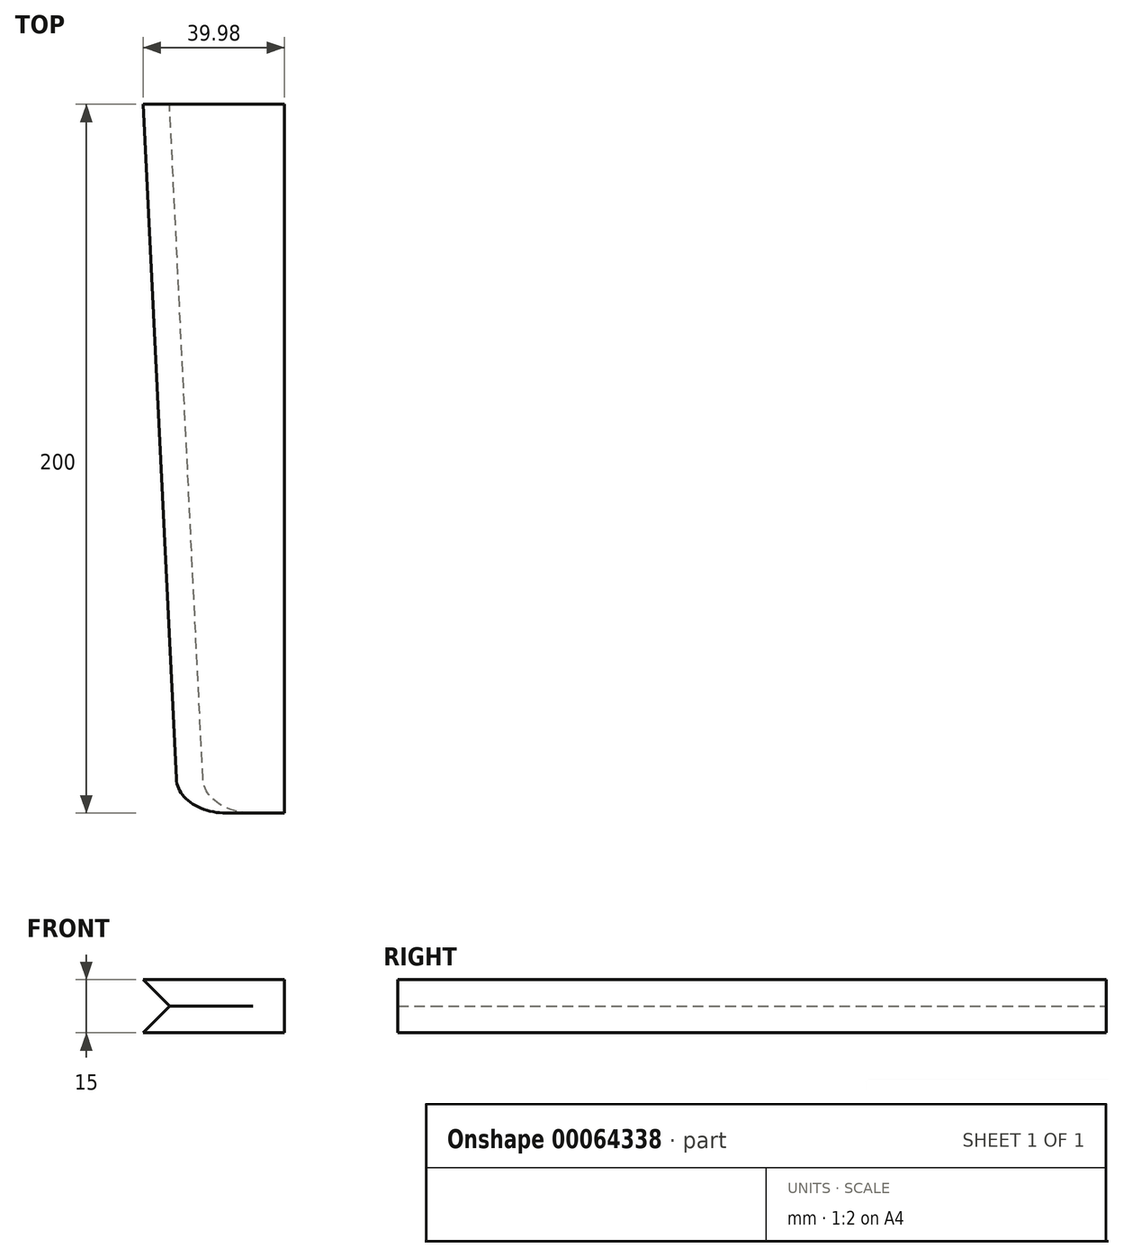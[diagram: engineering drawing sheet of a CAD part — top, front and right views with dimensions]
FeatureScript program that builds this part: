
annotation { "Feature Type Name" : "Feature", "Feature Type Description" : "" }
export const myFeature = defineFeature(function(context is Context, id is Id, definition is map)
    precondition{}
    {
        {
            var Q0;
            Q0=qCreatedBy(makeId("Front.planeOp"),FACE);
            var sketch = newSketch(context, id + "F0", { "sketchPlane" : qUnion([Q0])});
            skLineSegment(sketch, "E0", {"start": v(0, 0) * mm, "end": v(0, 15) * mm});
            skLineSegment(sketch, "E1", {"start": v(0, 15) * mm, "end": v(-40, 15) * mm});
            skLineSegment(sketch, "E2", {"start": v(-40, 15) * mm, "end": v(-32.5, 7.5) * mm});
            skLineSegment(sketch, "E3", {"start": v(-25, 0) * mm, "end": v(0, 0) * mm});
            skLineSegment(sketch, "E4", {"start": v(-32.5, 7.5) * mm, "end": v(-40, 0) * mm});
            skLineSegment(sketch, "E5", {"start": v(-40, 0) * mm, "end": v(-25, 0) * mm});
            skSolve(sketch);
        }
        {
            var Q0;
            Q0=makeQuery(id+"F0.imprint","IMPRINT",FACE,{"disambiguationData":[TD([[makeQuery(id+"F0.imprint","IMPRINT",EDGE,{"derivedFrom":sQuery(id+"F0.wireOp",EDGE,"E0")}),1.0]])]});
            extrude(context, id + "F1", {"entities" : qUnion([Q0]), "depth" : 200 * mm});
        }
        {
            var Q0;
            Q0=makeQuery(id+"F1.opExtrude","CAP_EDGE",EDGE,{"disambiguationData":[OSD([sQuery(id+"F0.wireOp",EDGE,"E2")])],"isStart":false});
            var Q1;
            Q1=makeQuery(id+"F1.opExtrude","CAP_EDGE",EDGE,{"disambiguationData":[OSD([sQuery(id+"F0.wireOp",EDGE,"E4")])],"isStart":false});
            chamfer(context, id + "F2", {"entities" : qUnion([Q0, Q1]), "chamferType" : ChamferType.OFFSET_ANGLE, "width" : 7 * mm, "oppositeDirection" : false, "angle" : 88 * degree, "tangentPropagation" : true});
        }
        {
            var Q0;
            {var subQ0=sQuery(id+"F0.wireOp",EDGE,"E2");Q0=makeQuery(id+"F2.opChamfer","BLEND_EDGE",EDGE,{"blendedFrom":[makeQuery(id+"F1.opExtrude","CAP_EDGE",EDGE,{"disambiguationData":[OSD([subQ0])],"isStart":false}),makeQuery(id+"F1.opExtrude","CAP_FACE",FACE,{"disambiguationData":[OSD([sQuery(id+"F0.wireOp",EDGE,"E0"),sQuery(id+"F0.wireOp",EDGE,"E1"),subQ0,sQuery(id+"F0.wireOp",EDGE,"E3")])],"isStart":false})],"blendedInto":[makeQuery(id+"F1.opExtrude","CAP_FACE",FACE,{"disambiguationData":[OSD([sQuery(id+"F0.wireOp",EDGE,"E0"),sQuery(id+"F0.wireOp",EDGE,"E1"),subQ0,sQuery(id+"F0.wireOp",EDGE,"E3")])],"isStart":false})]});}
            var Q1;
            {var subQ0=sQuery(id+"F0.wireOp",EDGE,"E4");Q1=makeQuery(id+"F2.opChamfer","BLEND_EDGE",EDGE,{"blendedFrom":[makeQuery(id+"F1.opExtrude","CAP_EDGE",EDGE,{"disambiguationData":[OSD([subQ0])],"isStart":false}),makeQuery(id+"F1.opExtrude","CAP_FACE",FACE,{"disambiguationData":[OSD([sQuery(id+"F0.wireOp",EDGE,"E0"),sQuery(id+"F0.wireOp",EDGE,"E1"),sQuery(id+"F0.wireOp",EDGE,"E2"),sQuery(id+"F0.wireOp",EDGE,"E3"),subQ0,sQuery(id+"F0.wireOp",EDGE,"E5")])],"isStart":false})],"blendedInto":[makeQuery(id+"F1.opExtrude","CAP_FACE",FACE,{"disambiguationData":[OSD([sQuery(id+"F0.wireOp",EDGE,"E0"),sQuery(id+"F0.wireOp",EDGE,"E1"),sQuery(id+"F0.wireOp",EDGE,"E2"),sQuery(id+"F0.wireOp",EDGE,"E3"),subQ0,sQuery(id+"F0.wireOp",EDGE,"E5")])],"isStart":false})]});}
            fillet(context, id + "F3", {"entities" : qUnion([Q0, Q1]), "radius" : 10 * mm, "tangentPropagation" : true, "allowEdgeOverflow" : false});
        }
    });
